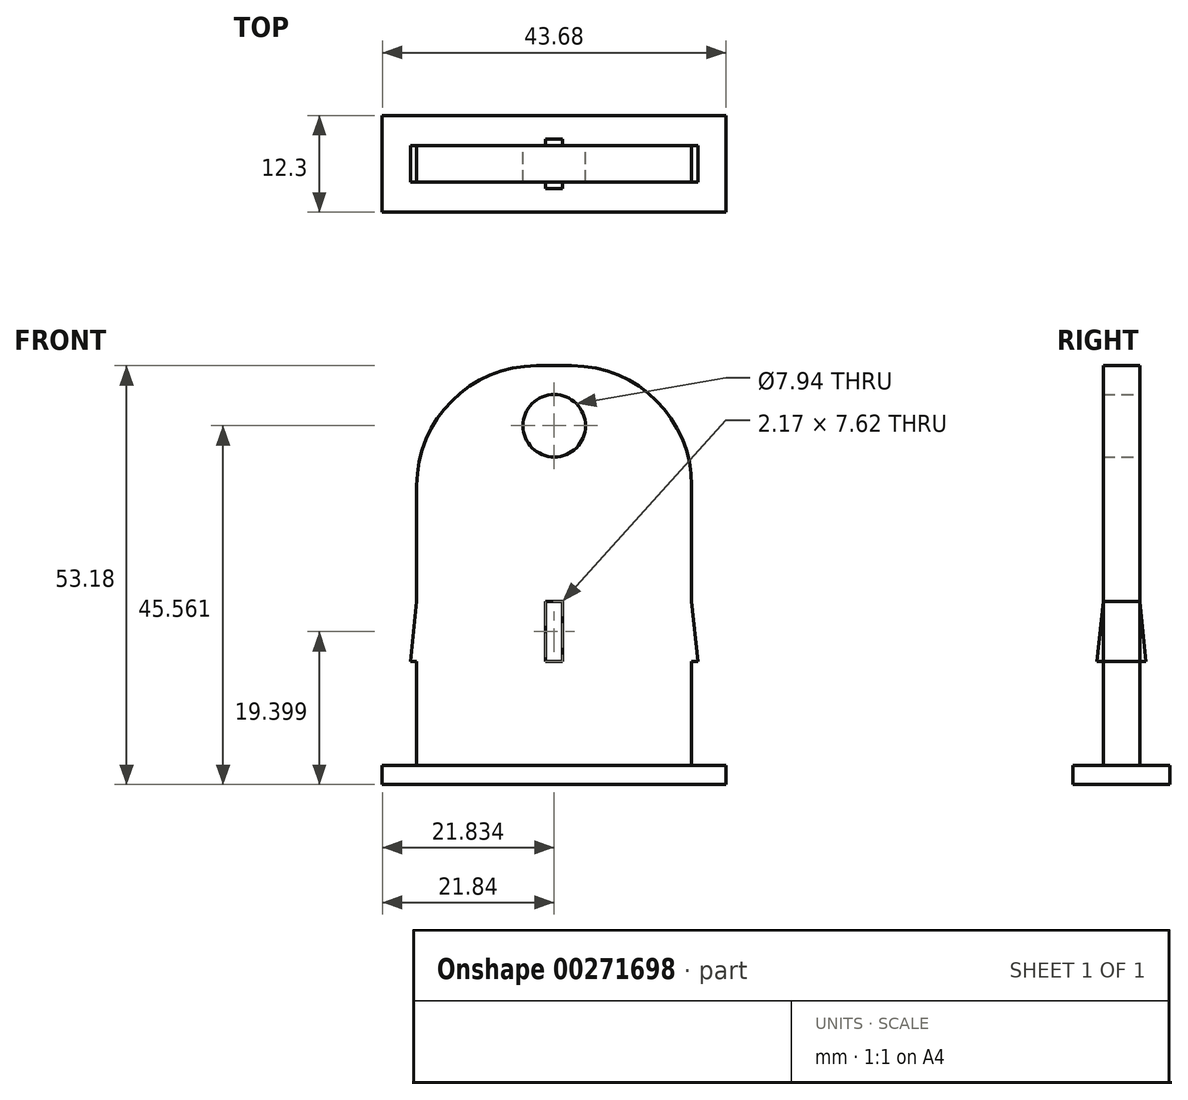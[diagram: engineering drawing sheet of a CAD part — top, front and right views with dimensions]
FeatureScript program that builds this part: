
annotation { "Feature Type Name" : "Feature", "Feature Type Description" : "" }
export const myFeature = defineFeature(function(context is Context, id is Id, definition is map)
    precondition{}
    {
        {
            var Q0;
            Q0=qCreatedBy(makeId("Top.planeOp"),FACE);
            var sketch = newSketch(context, id + "F0", { "sketchPlane" : qUnion([Q0])});
            skLineSegment(sketch, "E0.bottom", {"start": v(21.84, -6.15) * mm, "end": v(-21.84, -6.15) * mm});
            skLineSegment(sketch, "E0.top", {"start": v(21.84, 6.15) * mm, "end": v(-21.84, 6.15) * mm});
            skLineSegment(sketch, "E0.left", {"start": v(21.84, -6.15) * mm, "end": v(21.84, 6.15) * mm});
            skLineSegment(sketch, "E0.right", {"start": v(-21.84, -6.15) * mm, "end": v(-21.84, 6.15) * mm});
            skPoint(sketch, "E0.middle", {"position": v(0, 0) * mm});
            skSolve(sketch);
        }
        {
            var Q0;
            Q0 = qSketchRegion(id + "F0", true);
            extrude(context, id + "F1", {"entities" : qUnion([Q0]), "depth" : 2.38 * mm});
        }
        {
            var Q0;
            Q0=makeQuery(id+"F1.opExtrude","CAP_FACE",FACE,{"disambiguationData":[OSD([sQuery(id+"F0.wireOp",EDGE,"E0.bottom"),sQuery(id+"F0.wireOp",EDGE,"E0.top"),sQuery(id+"F0.wireOp",EDGE,"E0.left"),sQuery(id+"F0.wireOp",EDGE,"E0.right")])],"isStart":false});
            var sketch = newSketch(context, id + "F2", { "sketchPlane" : qUnion([Q0])});
            skLineSegment(sketch, "E1.bottom", {"start": v(17.46, 2.31) * mm, "end": v(-17.46, 2.31) * mm});
            skLineSegment(sketch, "E1.top", {"start": v(17.46, -2.31) * mm, "end": v(-17.46, -2.31) * mm});
            skLineSegment(sketch, "E1.left", {"start": v(17.46, 2.31) * mm, "end": v(17.46, -2.31) * mm});
            skLineSegment(sketch, "E1.right", {"start": v(-17.46, 2.31) * mm, "end": v(-17.46, -2.31) * mm});
            skPoint(sketch, "E1.middle", {"position": v(0, 0) * mm});
            skSolve(sketch);
        }
        {
            var Q0;
            Q0 = qSketchRegion(id + "F2", true);
            extrude(context, id + "F3", {"entities" : qUnion([Q0]), "operationType" : NewBodyOperationType.ADD, "depth" : 50.8 * mm});
        }
        {
            var Q0;
            Q0=makeQuery(id+"F3.opExtrude","CAP_EDGE",EDGE,{"disambiguationData":[OSD([sQuery(id+"F2.wireOp",EDGE,"E1.right")])],"isStart":false});
            var Q1;
            Q1=makeQuery(id+"F3.opExtrude","CAP_EDGE",EDGE,{"disambiguationData":[OSD([sQuery(id+"F2.wireOp",EDGE,"E1.left")])],"isStart":false});
            fillet(context, id + "F4", {"entities" : qUnion([Q0, Q1]), "radius" : 15.24 * mm, "tangentPropagation" : true, "allowEdgeOverflow" : false});
        }
        {
            var Q0;
            Q0=makeQuery(id+"F3.opExtrude","SWEPT_FACE",FACE,{"disambiguationData":[OSD([sQuery(id+"F2.wireOp",EDGE,"E1.bottom")])]});
            var sketch = newSketch(context, id + "F5", { "sketchPlane" : qUnion([Q0])});
            skCircle(sketch, "E2", {"center": v(0, 45.56) * mm, "radius": 3.97 * mm});
            skSolve(sketch);
        }
        {
            var Q0;
            Q0 = qSketchRegion(id + "F5", true);
            extrude(context, id + "F6", {"entities" : qUnion([Q0]), "operationType" : NewBodyOperationType.REMOVE, "endBound" : BoundingType.THROUGH_ALL, "oppositeDirection" : true, "depth" : 25.4 * mm});
        }
        {
            var Q0;
            Q0=makeQuery(id+"F3.opExtrude","SWEPT_FACE",FACE,{"disambiguationData":[OSD([sQuery(id+"F2.wireOp",EDGE,"E1.top")])]});
            var sketch = newSketch(context, id + "F7", { "sketchPlane" : qUnion([Q0])});
            skLineSegment(sketch, "E3", {"start": v(17.46, 23.2) * mm, "end": v(18.28, 15.59) * mm});
            skLineSegment(sketch, "E4", {"start": v(18.28, 15.59) * mm, "end": v(17.46, 15.59) * mm});
            skLineSegment(sketch, "E5", {"start": v(17.46, 15.59) * mm, "end": v(17.46, 23.2) * mm});
            skSolve(sketch);
        }
        {
            var Q0;
            Q0 = qSketchRegion(id + "F7", true);
            var Q1;
            Q1=makeQuery(id+"F3.opExtrude","SWEPT_FACE",FACE,{"disambiguationData":[OSD([sQuery(id+"F2.wireOp",EDGE,"E1.bottom")])]});
            extrude(context, id + "F8", {"entities" : qUnion([Q0]), "operationType" : NewBodyOperationType.ADD, "endBound" : BoundingType.UP_TO_SURFACE, "oppositeDirection" : true, "endBoundEntityFace" : qUnion([Q1]), "depth" : 25.4 * mm});
        }
        {
            var Q0;
            Q0=makeQuery(id+"F1.opExtrude","SWEPT_BODY",BODY,{"disambiguationData":[OSD([sQuery(id+"F0.wireOp",EDGE,"E0.bottom"),sQuery(id+"F0.wireOp",EDGE,"E0.top"),sQuery(id+"F0.wireOp",EDGE,"E0.left"),sQuery(id+"F0.wireOp",EDGE,"E0.right")])]});
            var Q1;
            Q1=qCreatedBy(makeId("Right.planeOp"),FACE);
            mirror(context, id + "F9", {"operationType" : NewBodyOperationType.ADD, "entities" : qUnion([Q0]), "mirrorPlane" : qUnion([Q1])});
        }
        {
            var Q0;
            Q0=qCreatedBy(makeId("Right.planeOp"),FACE);
            var sketch = newSketch(context, id + "F10", { "sketchPlane" : qUnion([Q0])});
            skLineSegment(sketch, "E6", {"start": v(-2.31, 15.59) * mm, "end": v(-3.12, 15.59) * mm});
            skLineSegment(sketch, "E7", {"start": v(-3.12, 15.59) * mm, "end": v(-2.31, 23.2) * mm});
            skLineSegment(sketch, "E8", {"start": v(-2.31, 23.2) * mm, "end": v(-2.31, 15.59) * mm});
            skLineSegment(sketch, "E9", {"start": v(2.31, 23.2) * mm, "end": v(2.31, 15.59) * mm});
            skLineSegment(sketch, "E10", {"start": v(2.31, 15.59) * mm, "end": v(3.12, 15.59) * mm});
            skLineSegment(sketch, "E11", {"start": v(3.12, 15.59) * mm, "end": v(2.31, 23.2) * mm});
            skSolve(sketch);
        }
        {
            var Q0;
            Q0 = qSketchRegion(id + "F10", true);
            extrude(context, id + "F11", {"entities" : qUnion([Q0]), "operationType" : NewBodyOperationType.ADD, "depth" : 1.08 * mm, "hasSecondDirection" : true, "secondDirectionOppositeDirection" : true, "secondDirectionDepth" : 1.1 * mm});
        }
    });
